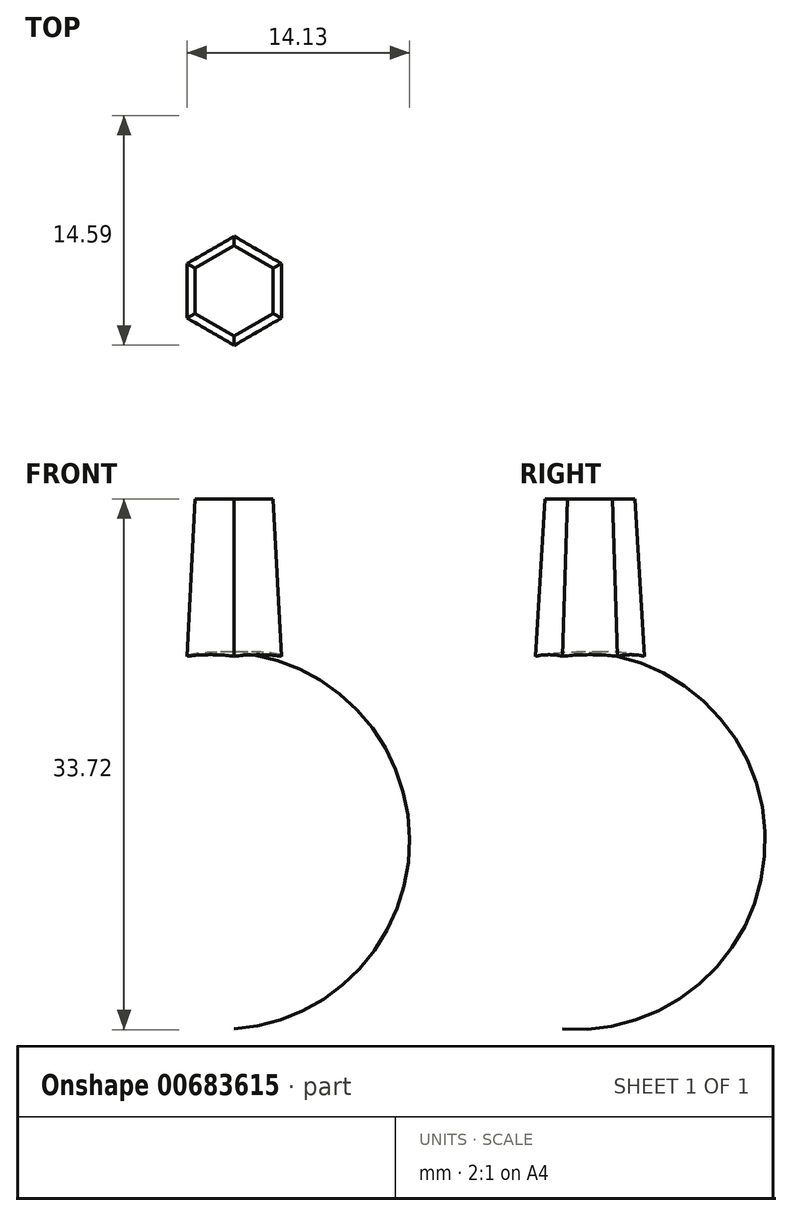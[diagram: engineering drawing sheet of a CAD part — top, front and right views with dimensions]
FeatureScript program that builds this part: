
annotation { "Feature Type Name" : "Feature", "Feature Type Description" : "" }
export const myFeature = defineFeature(function(context is Context, id is Id, definition is map)
    precondition{}
    {
        {
            var Q0;
            Q0=qCreatedBy(makeId("Top.planeOp"),FACE);
            var sketch = newSketch(context, id + "F0", { "sketchPlane" : qUnion([Q0])});
            skCircle(sketch, "E0.cCircle", {"center": v(0, 0) * mm, "radius": 3 * mm, "construction": true});
            skLineSegment(sketch, "E0.0", {"start": v(3, 1.73) * mm, "end": v(3, -1.73) * mm});
            skLineSegment(sketch, "E0.1", {"start": v(3, -1.73) * mm, "end": v(0, -3.46) * mm});
            skLineSegment(sketch, "E0.2", {"start": v(0, -3.46) * mm, "end": v(-3, -1.73) * mm});
            skLineSegment(sketch, "E0.3", {"start": v(-3, -1.73) * mm, "end": v(-3, 1.73) * mm});
            skLineSegment(sketch, "E0.4", {"start": v(-3, 1.73) * mm, "end": v(0, 3.46) * mm});
            skLineSegment(sketch, "E0.5", {"start": v(0, 3.46) * mm, "end": v(3, 1.73) * mm});
            skPoint(sketch, "E0.0.midPoint", {"position": v(3, 0) * mm});
            skSolve(sketch);
        }
        {
            var Q0;
            Q0=makeQuery(id+"F0.imprint","IMPRINT",FACE,{"disambiguationData":[TD([[makeQuery(id+"F0.imprint","IMPRINT",EDGE,{"derivedFrom":sQuery(id+"F0.wireOp",EDGE,"E0.0")}),-1.0]])]});
            extrude(context, id + "F1", {"entities" : qUnion([Q0]), "depth" : 10 * mm, "offsetDistance" : 25 * mm, "hasDraft" : true, "draftAngle" : 3 * degree, "draftPullDirection" : true});
        }
        {
            var Q0;
            Q0=qCreatedBy(makeId("Origin.pointOp"),VERTEX);
            var Q1;
            Q1=makeQuery(id+"F1.opExtrude","CAP_VERTEX",VERTEX,{"disambiguationData":[OSD([sQuery(id+"F0.wireOp",EDGE,"E0.3"),sQuery(id+"F0.wireOp",EDGE,"E0.4")])],"isStart":true});
            var Q2;
            Q2=makeQuery(id+"F1.opExtrude","CAP_VERTEX",VERTEX,{"disambiguationData":[OSD([sQuery(id+"F0.wireOp",EDGE,"E0.3"),sQuery(id+"F0.wireOp",EDGE,"E0.4")])],"isStart":false});
            cPlane(context, id + "F2", {"entities" : qUnion([Q0, Q1, Q2]), "cplaneType" : CPlaneType.THREE_POINT, "offset" : 25 * mm, "width" : 150 * mm, "height" : 150 * mm});
        }
        {
            var Q0;
            Q0=qCreatedBy(id+"F2.planeOp",FACE);
            var sketch = newSketch(context, id + "F3", { "sketchPlane" : qUnion([Q0])});
            skPoint(sketch, "E1.0", {"position": v(-3.46, 0) * mm});
            skArc(sketch, "E2", {"start": v(0, 0.25) * mm, "mid": v(-1.74, 0.25) * mm, "end": v(-3.46, 0) * mm});
            skLineSegment(sketch, "E3", {"start": v(-3.46, 0) * mm, "end": v(0, 0) * mm});
            skLineSegment(sketch, "E4", {"start": v(0, 0.25) * mm, "end": v(0, 0) * mm});
            skSolve(sketch);
        }
        {
            var Q0;
            Q0=makeQuery(id+"F3.imprint","IMPRINT",FACE,{"disambiguationData":[TD([[makeQuery(id+"F3.imprint","IMPRINT",EDGE,{"derivedFrom":sQuery(id+"F3.wireOp",EDGE,"E2")}),1.0]])]});
            var Q1;
            Q1=sQuery(id+"F3.wireOp",EDGE,"E4");
            revolve(context, id + "F4", {"entities" : qUnion([Q0]), "axis" : qUnion([Q1]), "revolveType" : RevolveType.FULL});
        }
        {
            var Q0;
            Q0=makeQuery(id+"F4.opRevolve","SWEPT_BODY",BODY,{"disambiguationData":[OSD([sQuery(id+"F3.wireOp",EDGE,"E2"),sQuery(id+"F3.wireOp",EDGE,"E3"),sQuery(id+"F3.wireOp",EDGE,"E4")])]});
            var Q1;
            Q1=makeQuery(id+"F1.opExtrude","SWEPT_BODY",BODY,{"disambiguationData":[OSD([sQuery(id+"F0.wireOp",EDGE,"E0.0"),sQuery(id+"F0.wireOp",EDGE,"E0.1"),sQuery(id+"F0.wireOp",EDGE,"E0.2"),sQuery(id+"F0.wireOp",EDGE,"E0.3"),sQuery(id+"F0.wireOp",EDGE,"E0.4"),sQuery(id+"F0.wireOp",EDGE,"E0.5")])]});
            booleanBodies(context, id + "F5", {"operationType" : BooleanOperationType.SUBTRACTION, "tools" : qUnion([Q0]), "targets" : qUnion([Q1])});
        }
    });
